FCSTD DOCUMENT  (FreeCAD 0.14R2935 (Git))
Label: essai
License: CC-BY 3.0
LicenseURL: http://creativecommons.org/licenses/by/3.0/
objects: Sketcher::SketchObject×1
note: 1 computed .brp shape members not serialized (recipe doc carries the construction recipe); baked Part::Feature solids carry a one-line shape summary decoded from their .brp

FEATURE [Sketcher::SketchObject] Sketch
  sketch-geometry (9):
    g0: LineSegment StartX=-11.5055 StartY=6 StartZ=0 EndX=7.49448 EndY=6 EndZ=0
    g1: LineSegment StartX=7.49448 StartY=0 StartZ=0 EndX=3.49448 EndY=0 EndZ=0
    g2: LineSegment StartX=-11.5055 StartY=0 StartZ=0 EndX=-11.5055 EndY=6 EndZ=0
    g3: LineSegment StartX=7.49448 StartY=6 StartZ=0 EndX=7.49448 EndY=0 EndZ=0
    g4: LineSegment StartX=-11.7437 StartY=-0.046273 StartZ=0 EndX=-7.74365 EndY=-0.046273 EndZ=0
    g5: LineSegment StartX=3.49448 StartY=0 StartZ=0 EndX=3.49448 EndY=-10 EndZ=0
    g6: LineSegment StartX=-0.50552 StartY=-10 StartZ=0 EndX=3.49448 EndY=-10 EndZ=0
    g7: LineSegment StartX=-0.770125 StartY=-10.0726 StartZ=0 EndX=-0.770125 EndY=0 EndZ=0
    g8: LineSegment StartX=-0.770125 StartY=0 StartZ=0 EndX=-3.77013 EndY=0 EndZ=0
  constraints (24):
    c: Horizontal(g0)
    c: PointOnObject(g1,g-1)
    c: Coincident(g2,g0)
    c: Horizontal(g1)
    c: Vertical(g2)
    c: Coincident(g1,g3)
    c: Coincident(g0,g3)
    c: Vertical(g3)
    c: DistanceX(g0) = 19
    c: DistanceX(g1) = -4
    c: Horizontal(g4)
    c: DistanceX(g4) = 4
    c: Coincident(g5,g1)
    c: Vertical(g5)
    c: DistanceY(g5) = -10
    c: Coincident(g6,g5)
    c: Horizontal(g6)
    c: DistanceX(g6) = 4
    c: PointOnObject(g7,g-1)
    c: Vertical(g7)
    c: Coincident(g8,g7)
    c: PointOnObject(g8,g-1)
    c: Horizontal(g8)
    c: DistanceX(g8) = -3
